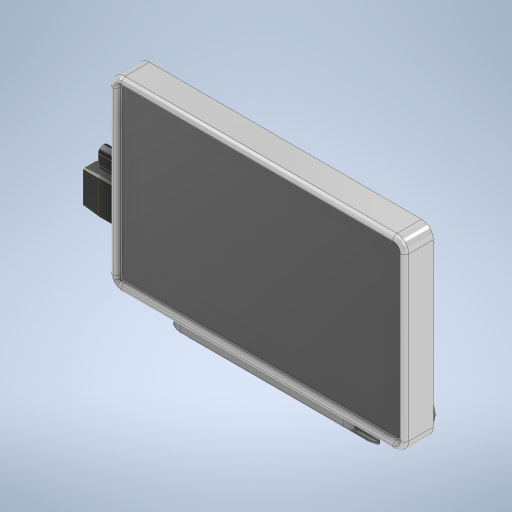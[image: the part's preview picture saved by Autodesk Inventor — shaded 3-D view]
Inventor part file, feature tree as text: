
AUTODESK INVENTOR PART (.ipt)
format: ipt  version: 2023 (Build 270158030, 158C)  size: 1,255,936 bytes
history: native  units: mm
features: extrude x26, sketch x24, fillet x22, projected_geometry x15, other x11, hole x6, chamfer x1
ambient origin geometry x8: Origin, YZ Plane, XZ Plane, XY Plane, X Axis, Y Axis, Z Axis, Center Point
bodies: Body1 (feature_tree), Body2 (feature_tree), Body3 (feature_tree), Body4 (feature_tree), Body5 (feature_tree), Body6 (feature_tree)
feature tree (105):
  other  "Monitor"
  extrude  "Extrusion1"  Depth=100.0mm
  extrude  "Extrusion2"  Depth=50.0mm
  other  "Work Point1"
  other  "Work Point2"
  other  "Work Point3"
  other  "Work Point4"
  hole  "Hole1"  [1 undecoded]
  hole  "Hole2"  [1 undecoded]
  hole  "Hole3"  [1 undecoded]
  hole  "Hole4"  [1 undecoded]
  fillet  "Fillet1"  Radius=15.0mm
  extrude  "Extrusion3"  Depth=9.15mm
  fillet  "Fillet2"  Radius=1.0mm
  extrude  "Extrusion4"  Depth=3.0mm
  extrude  "Extrusion5"  Depth=6.0mm
  fillet  "Fillet3"  Radius=8.15mm
  fillet  "Fillet4"  Radius=2.7mm
  extrude  "Extrusion6"  Depth=6.0mm
  extrude  "Extrusion7"  Depth=15.0mm
  extrude  "Extrusion8"  Depth=4.19mm
  extrude  "Extrusion9"  Depth=1.5mm
  extrude  "Extrusion10"  Depth=2.5mm
  extrude  "Extrusion11"  Depth=2.11mm
  fillet  "Fillet5"  Radius=0.45mm
  fillet  "Fillet6"  Radius=0.45mm
  extrude  "Extrusion22"  Depth=0.45mm
  other  "Work Point5"
  extrude  "Extrusion23"  Depth=0.45mm
  fillet  "Fillet22"  Radius=0.4mm
  extrude  "Extrusion24"  Depth=0.2mm
  extrude  "Extrusion25"  Depth=12.0mm TaperAngle=0.0deg
  extrude  "Extrusion26"  Depth=3.0mm
  extrude  "Extrusion12"  Depth=3.0mm
  extrude  "Extrusion13"  Depth=3.0mm
  sketch  "Sketch15"  dims[d58=3.0mm d59=0.0mm d60=15.0mm]
  hole  "Hole6"  [1 undecoded]
  fillet  "Fillet7"  Radius=7.5mm
  extrude  "Extrusion14"  Depth=2.0mm TaperAngle=0.0deg
  chamfer  "Chamfer1"  Distance=4.9mm
  fillet  "Fillet8"  Radius=0.73mm
  fillet  "Fillet20"  Radius=2.55mm
  fillet  "Fillet9"  Radius=39.0mm
  extrude  "Extrusion15"  Depth=3.0mm TaperAngle=0.0deg
  extrude  "Extrusion16"  Depth=3.0mm
  fillet  "Fillet10"  Radius=3.175mm
  fillet  "Fillet11"  Radius=5.0mm
  extrude  "Extrusion17"  Depth=3.0mm TaperAngle=0.0deg
  extrude  "Extrusion18"  Depth=3.0mm
  extrude  "Extrusion19"  Depth=3.0mm
  hole  "Hole7"  [1 undecoded]
  fillet  "Fillet12"  Radius=18.6mm
  extrude  "Extrusion20"  Depth=3.0mm
  extrude  "Extrusion21"  Depth=3.0mm
  fillet  "Fillet14"  Radius=5.09mm
  fillet  "Fillet15"  Radius=3.0mm
  fillet  "Fillet16"  Radius=0.2mm
  fillet  "Fillet17"  Radius=5.0mm
  fillet  "Fillet18"  Radius=5.0mm
  fillet  "Fillet19"  Radius=5.0mm
  fillet  "Fillet21"  Radius=5.0mm
  fillet  "Fillet23"  Radius=12.0mm
  sketch  "Sketch1"  dims[d0=165.0mm d1=100.0mm]
  sketch  "Sketch2"  dims[d2=82.5mm d3=50.0mm]
  sketch  "Sketch4"  dims[d4=8.36mm d5=0.0mm d6=5.5mm]
  sketch  "Sketch5"  dims[d7=5.0mm d8=5.0mm]
  projected_geometry  "Projected Loop1"
  sketch  "Sketch6"  dims[d9=5.0mm d10=5.0mm]
  sketch  "Sketch7"  dims[d11=4.0mm d12=0.0mm]
  projected_geometry  "Projected Loop2"
  sketch  "Sketch8"  dims[d42=10.0mm d43=10.0mm d15=2.013mm d16=4.0mm d17=4.0mm d18=2.0mm d19=90.0deg d20=4.0mm d21=20.594885mm]
  sketch  "Sketch9"  dims[d24=10.0mm d25=10.0mm d26=2.013mm d27=4.0mm d28=4.0mm d29=2.0mm d30=90.0deg d31=4.0mm d32=20.594885mm]
  projected_geometry  "Projected Loop3"
  sketch  "Sketch10"  dims[d33=10.0mm d34=10.0mm d35=2.013mm d36=4.0mm d37=4.0mm d38=2.0mm d39=90.0deg d40=4.0mm d41=20.594885mm]
  sketch  "Sketch11"  dims[d44=10.0mm d45=10.0mm d46=2.013mm d47=4.0mm d48=4.0mm d49=2.0mm d50=90.0deg d51=4.0mm d52=20.594885mm d53=2.0mm d54=15.0mm]
  sketch  "Sketch12"  dims[d55=12.0mm d56=9.15mm d57=1.0mm]
  other  "case"
  projected_geometry  "Projected Loop4"
  projected_geometry  "Projected Loop5"
  projected_geometry  "Projected Loop6"
  sketch  "Sketch16"  dims[d61=12.0mm d62=6.0mm d63=8.15mm d64=4.075mm d65=2.7mm d66=0.0mm]
  projected_geometry  "Projected Loop7"
  sketch  "Sketch17"  dims[d67=6.0mm d68=0.5mm]
  projected_geometry  "Projected Loop8"
  projected_geometry  "Projected Loop9"
  projected_geometry  "Projected Loop10"
  other  "screws"
  sketch  "Sketch18"  dims[d69=0.5mm d70=15.0mm]
  sketch  "Sketch19"  dims[d71=6.3mm d72=4.19mm d73=0.7mm]
  sketch  "Sketch20"  dims[d74=1.5mm d75=1.5mm]
  other  "clip"
  sketch  "Sketch22"  dims[d76=20.5mm d77=2.5mm]
  projected_geometry  "Projected Loop11"
  sketch  "Sketch23"  dims[d78=2.5mm d79=2.11mm d80=0.45mm d81=0.45mm]
  sketch  "Sketch26"  dims[d82=0.45mm d83=0.45mm]
  projected_geometry  "Projected Loop12"
  other  "HDMI"
  sketch  "Sketch27"  dims[d84=0.45mm d85=0.45mm d86=0.4mm d87=0.0mm]
  sketch  "Sketch28"  dims[d88=0.5mm d89=0.2mm]
  projected_geometry  "Projected Loop13"
  sketch  "Sketch29"  dims[d90=4.5mm d91=0.0mm d92=12.0mm d93=0.0mm]
  projected_geometry  "Projected Loop14"
  other  "USB-C"
  sketch  "Sketch30"  dims[d94=9.1mm d95=3.2mm d96=0.1mm d97=43.0mm d98=0.35mm d99=7.5mm d100=0.0mm d101=2.0mm d102=0.0mm d103=4.9mm d104=0.73mm d105=2.55mm d106=39.0mm d107=14.0mm d108=0.0mm d109=6.35mm d110=3.175mm d111=5.0mm d112=12.0mm d113=0.0mm d114=38.0mm d115=18.0mm d116=38.0mm d117=18.6mm d118=7.67mm d119=21.67mm d120=5.09mm d121=0.0mm d122=3.0mm d123=0.2mm d124=5.0mm d125=5.0mm d126=5.0mm d127=5.0mm d128=12.0mm d130=12.0mm d132=2.0mm d133=0.0mm d134=16.0mm d135=19.0mm d136=2.0mm d139=2.0mm d141=2.0mm d143=2.0mm d145=2.0mm d146=2.0mm d147=5.0mm d148=0.7mm d149=8.0mm d150=8.0mm d151=0.7mm d152=0.7mm d154=15.0mm d155=0.0mm d167=2.9mm d168=6.0mm d169=5.5mm d170=0.5mm d171=90.0deg d172=7.6mm d173=20.594885mm d174=7.0mm d175=16.0mm d176=10.0mm d177=10.0mm d178=4.6mm d179=73.5mm d180=0.0mm d181=2.0mm d182=2.0mm d183=45.0deg d184=2.5mm d185=3.0mm d186=7.3mm d187=2.0mm d188=0.0mm d189=0.0mm d190=4.16mm d191=1.4mm d192=0.0mm d193=0.6mm d194=4.0mm d195=1.4mm d196=0.0mm d197=4.0mm d198=5.0mm d199=5.0mm d200=6.0mm d201=3.0mm d202=3.0mm d203=0.0mm d204=15.0mm d205=15.0mm d206=4.5mm d207=0.0mm d208=2.9mm d209=6.0mm d210=5.5mm d211=2.0mm d212=90.0deg d213=7.6mm d214=20.594885mm d215=10.0mm d216=24.180074mm d217=24.180074mm d218=14.0mm d219=0.0mm d221=0.7mm d223=1.5mm d225=10.0mm d227=1.5mm d228=2.0mm d229=1.9mm d230=1.5mm d231=14.0mm d232=0.0mm d233=10.0mm d234=2.0mm d235=4.0mm d236=1.0mm d237=1.5mm d238=4.0mm d240=0.7mm d241=0.7mm d242=0.5mm d244=24.180074mm d245=1.65mm d246=11.165mm d247=3.0mm d248=2.45mm d249=2.45mm d250=0.0mm d251=0.0mm d252=21.0mm d253=10.5mm d254=2.9mm d255=2.9mm d256=3.45mm d257=3.45mm d258=17.6mm d259=0.0mm d260=2.0mm d261=10.0mm d262=-0.872665mm d263=2.4mm d264=2.4mm d265=0.0mm d266=0.0mm d267=6.2mm d268=12.1mm d269=18.6mm d270=0.0mm d271=0.5mm d272=3.0mm]
  projected_geometry  "Projected Loop15"
note: 6 required parameter values undecoded (feature->parameter linkage not recoverable at this tier; creation-order binding heuristic only, values carry confidence <= 0.55)
